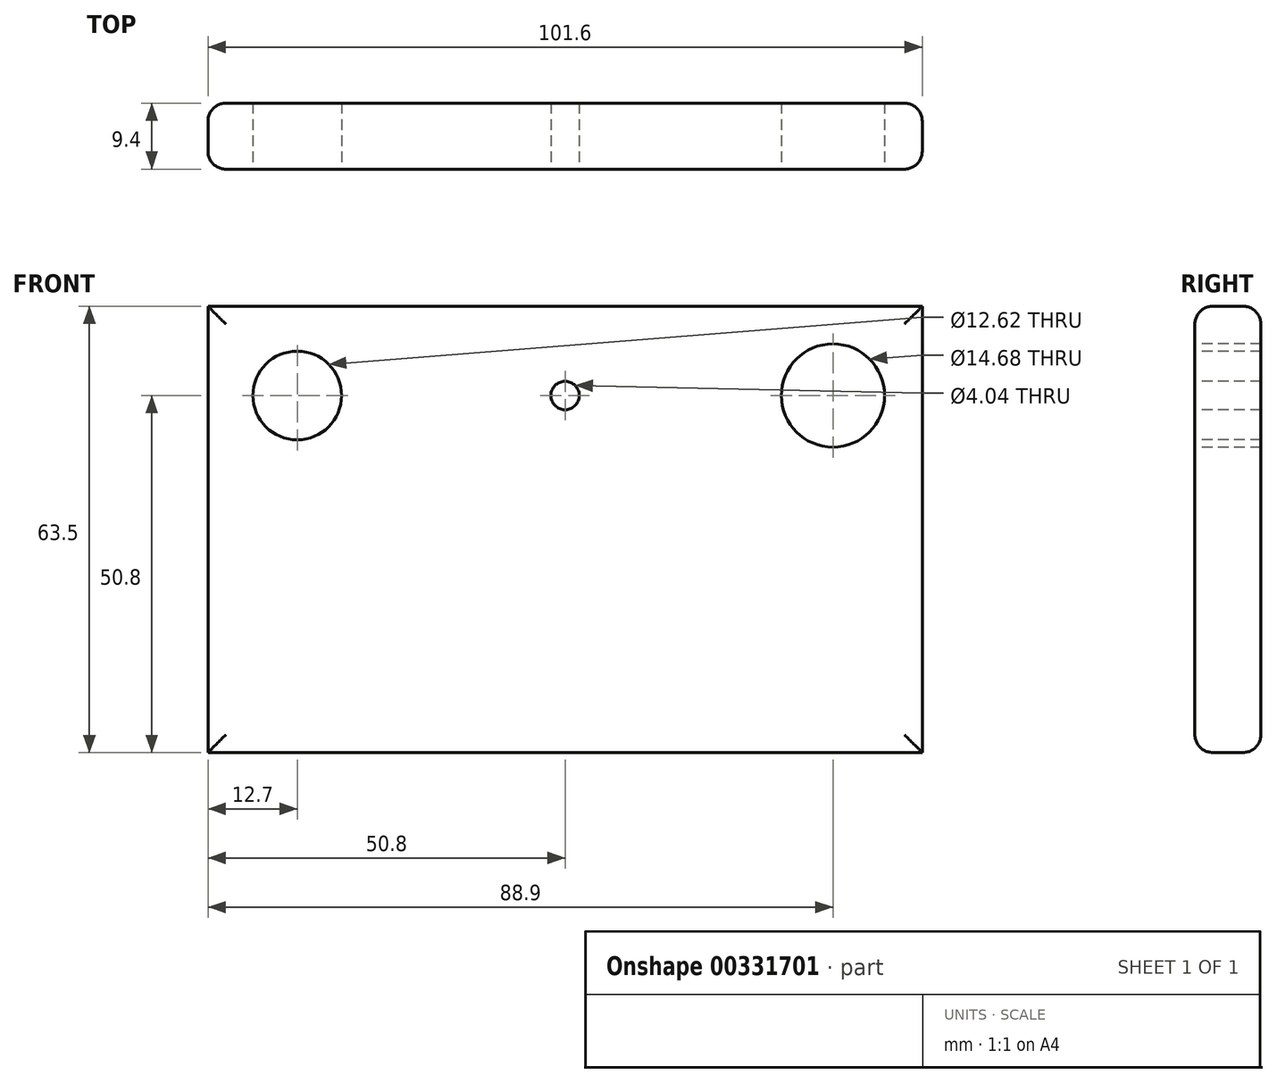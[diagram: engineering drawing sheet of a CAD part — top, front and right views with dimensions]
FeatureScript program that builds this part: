
annotation { "Feature Type Name" : "Feature", "Feature Type Description" : "" }
export const myFeature = defineFeature(function(context is Context, id is Id, definition is map)
    precondition{}
    {
        {
            var Q0;
            Q0=qCreatedBy(makeId("Front.planeOp"),FACE);
            var sketch = newSketch(context, id + "F0", { "sketchPlane" : qUnion([Q0])});
            skLineSegment(sketch, "E0.bottom", {"start": v(50.8, -31.75) * mm, "end": v(-50.8, -31.75) * mm});
            skLineSegment(sketch, "E0.top", {"start": v(50.8, 31.75) * mm, "end": v(-50.8, 31.75) * mm});
            skLineSegment(sketch, "E0.left", {"start": v(50.8, -31.75) * mm, "end": v(50.8, 31.75) * mm});
            skLineSegment(sketch, "E0.right", {"start": v(-50.8, -31.75) * mm, "end": v(-50.8, 31.75) * mm});
            skPoint(sketch, "E0.middle", {"position": v(0, 0) * mm});
            skSolve(sketch);
        }
        {
            var Q0;
            Q0=makeQuery(id+"F0.imprint","IMPRINT",FACE,{"disambiguationData":[TD([[makeQuery(id+"F0.imprint","IMPRINT",EDGE,{"derivedFrom":sQuery(id+"F0.wireOp",EDGE,"E0.bottom")}),-1.0]])]});
            extrude(context, id + "F1", {"entities" : qUnion([Q0]), "depth" : 9.4 * mm});
        }
        {
            var Q0;
            Q0=makeQuery(id+"F1.opExtrude","CAP_FACE",FACE,{"disambiguationData":[OSD([sQuery(id+"F0.wireOp",EDGE,"E0.bottom"),sQuery(id+"F0.wireOp",EDGE,"E0.top"),sQuery(id+"F0.wireOp",EDGE,"E0.left"),sQuery(id+"F0.wireOp",EDGE,"E0.right")])],"isStart":false});
            var sketch = newSketch(context, id + "F2", { "sketchPlane" : qUnion([Q0])});
            skPoint(sketch, "E1", {"position": v(-38.1, 19.05) * mm});
            skPoint(sketch, "E2", {"position": v(38.1, 19.05) * mm});
            skPoint(sketch, "E3", {"position": v(0, 19.05) * mm});
            skSolve(sketch);
        }
        {
            var Q0;
            Q0=sQuery(id+"F2.wireOp",VERTEX,"E1");
            var Q1;
            Q1=makeQuery(id+"F1.opExtrude","SWEPT_BODY",BODY,{"disambiguationData":[OSD([sQuery(id+"F0.wireOp",EDGE,"E0.bottom"),sQuery(id+"F0.wireOp",EDGE,"E0.top"),sQuery(id+"F0.wireOp",EDGE,"E0.left"),sQuery(id+"F0.wireOp",EDGE,"E0.right")])]});
            hole(context, id + "F3", {"style" : HoleStyle.SIMPLE, "endStyle" : HoleEndStyle.THROUGH, "holeDiameter" : 12.62 * mm, "tappedDepth" : 19.38 * mm, "tapClearance" : 3, "startFromSketch" : true, "locations" : qUnion([Q0]), "scope" : qUnion([Q1])});
        }
        {
            var Q0;
            Q0=sQuery(id+"F2.wireOp",VERTEX,"E2");
            var Q1;
            Q1=makeQuery(id+"F1.opExtrude","SWEPT_BODY",BODY,{"disambiguationData":[OSD([sQuery(id+"F0.wireOp",EDGE,"E0.bottom"),sQuery(id+"F0.wireOp",EDGE,"E0.top"),sQuery(id+"F0.wireOp",EDGE,"E0.left"),sQuery(id+"F0.wireOp",EDGE,"E0.right")])]});
            hole(context, id + "F4", {"style" : HoleStyle.SIMPLE, "endStyle" : HoleEndStyle.THROUGH, "holeDiameter" : 14.68 * mm, "tappedDepth" : 19.38 * mm, "tapClearance" : 3, "startFromSketch" : true, "locations" : qUnion([Q0]), "scope" : qUnion([Q1])});
        }
        {
            var Q0;
            Q0=makeQuery(id+"F1.opExtrude","CAP_EDGE",EDGE,{"disambiguationData":[OSD([sQuery(id+"F0.wireOp",EDGE,"E0.top")])],"isStart":false});
            var Q1;
            Q1=makeQuery(id+"F1.opExtrude","CAP_EDGE",EDGE,{"disambiguationData":[OSD([sQuery(id+"F0.wireOp",EDGE,"E0.right")])],"isStart":false});
            var Q2;
            Q2=makeQuery(id+"F1.opExtrude","CAP_EDGE",EDGE,{"disambiguationData":[OSD([sQuery(id+"F0.wireOp",EDGE,"E0.left")])],"isStart":false});
            var Q3;
            Q3=makeQuery(id+"F1.opExtrude","CAP_EDGE",EDGE,{"disambiguationData":[OSD([sQuery(id+"F0.wireOp",EDGE,"E0.bottom")])],"isStart":false});
            var Q4;
            Q4=makeQuery(id+"F1.opExtrude","CAP_EDGE",EDGE,{"disambiguationData":[OSD([sQuery(id+"F0.wireOp",EDGE,"E0.left")])],"isStart":true});
            var Q5;
            Q5=makeQuery(id+"F1.opExtrude","CAP_EDGE",EDGE,{"disambiguationData":[OSD([sQuery(id+"F0.wireOp",EDGE,"E0.right")])],"isStart":true});
            var Q6;
            Q6=makeQuery(id+"F1.opExtrude","CAP_EDGE",EDGE,{"disambiguationData":[OSD([sQuery(id+"F0.wireOp",EDGE,"E0.bottom")])],"isStart":true});
            var Q7;
            Q7=makeQuery(id+"F1.opExtrude","CAP_EDGE",EDGE,{"disambiguationData":[OSD([sQuery(id+"F0.wireOp",EDGE,"E0.top")])],"isStart":true});
            fillet(context, id + "F5", {"entities" : qUnion([Q0, Q1, Q2, Q3, Q4, Q5, Q6, Q7]), "radius" : 2.54 * mm, "tangentPropagation" : true, "allowEdgeOverflow" : false});
        }
        {
            var Q0;
            Q0=sQuery(id+"F2.wireOp",VERTEX,"E3");
            var Q1;
            Q1=makeQuery(id+"F1.opExtrude","SWEPT_BODY",BODY,{"disambiguationData":[OSD([sQuery(id+"F0.wireOp",EDGE,"E0.bottom"),sQuery(id+"F0.wireOp",EDGE,"E0.top"),sQuery(id+"F0.wireOp",EDGE,"E0.left"),sQuery(id+"F0.wireOp",EDGE,"E0.right")])]});
            hole(context, id + "F6", {"style" : HoleStyle.SIMPLE, "endStyle" : HoleEndStyle.THROUGH, "standardTappedOrClearance" : lookupTablePath({ "standard" : "ANSI", "engagement" : "75%", "pitch" : "32 tpi", "size" : "#10", "type" : "Tapped" }), "standardBlindInLast" : lookupTablePath({ "standard" : "ANSI", "engagement" : "75%", "pitch" : "32 tpi", "size" : "#10", "type" : "Tapped" }), "holeDiameter" : 4.04 * mm, "showTappedDepth" : true, "tappedDepth" : 19.38 * mm, "tapClearance" : 3, "startFromSketch" : true, "locations" : qUnion([Q0]), "scope" : qUnion([Q1]), "majorDiameter" : 4.83 * mm});
        }
    });
